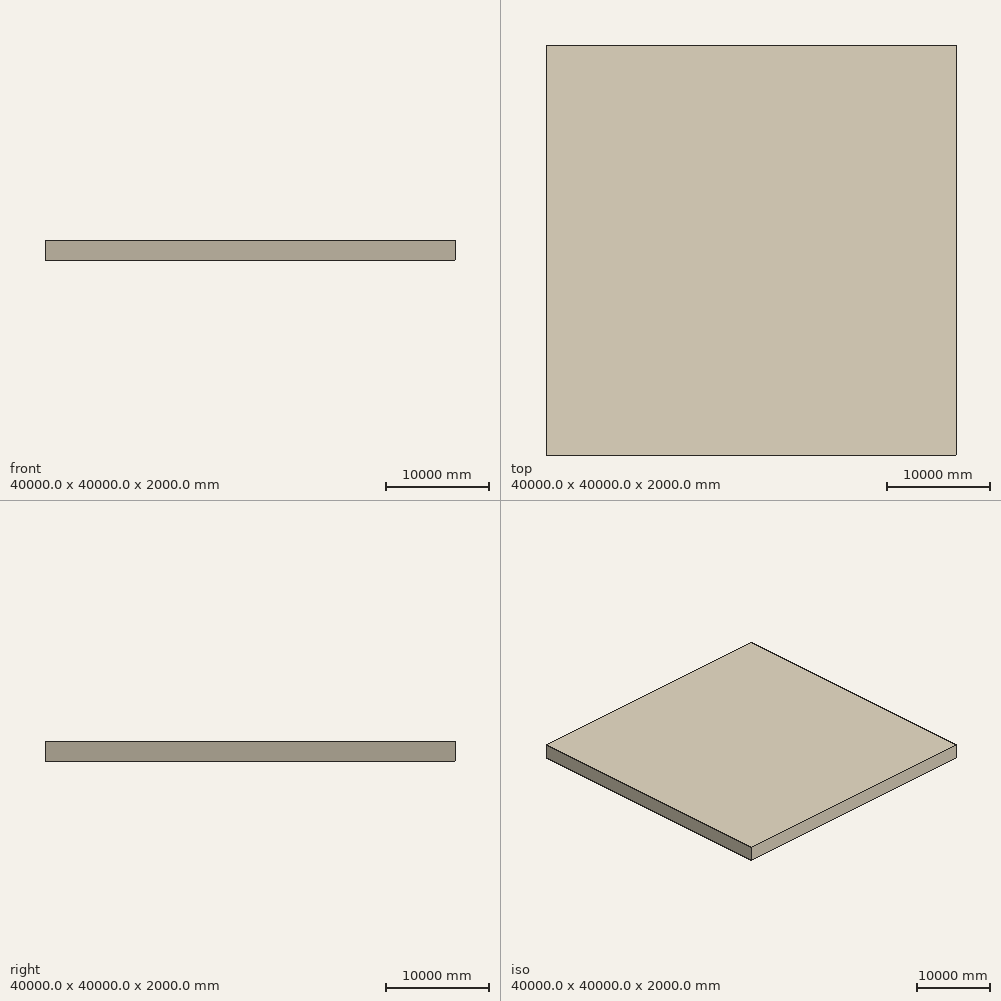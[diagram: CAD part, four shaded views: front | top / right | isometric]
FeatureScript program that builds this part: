
annotation { "Feature Type Name" : "Feature", "Feature Type Description" : "" }
export const myFeature = defineFeature(function(context is Context, id is Id, definition is map)
    precondition{}
    {
        {
            var Q0;
            Q0=qCreatedBy(makeId("Top.planeOp"),FACE);
            var sketch = newSketch(context, id + "F0", { "sketchPlane" : qUnion([Q0])});
            skLineSegment(sketch, "E0.bottom", {"start": v(-20000, 20000) * mm, "end": v(20000, 20000) * mm});
            skLineSegment(sketch, "E0.top", {"start": v(-20000, -20000) * mm, "end": v(20000, -20000) * mm});
            skLineSegment(sketch, "E0.left", {"start": v(-20000, 20000) * mm, "end": v(-20000, -20000) * mm});
            skLineSegment(sketch, "E0.right", {"start": v(20000, 20000) * mm, "end": v(20000, -20000) * mm});
            skPoint(sketch, "E0.middle", {"position": v(0, 0) * mm});
            skSolve(sketch);
        }
        {
            var Q0;
            Q0 = qSketchRegion(id + "F0", true);
            extrude(context, id + "F1", {"entities" : qUnion([Q0]), "oppositeDirection" : true, "depth" : 2000 * mm});
        }
    });
